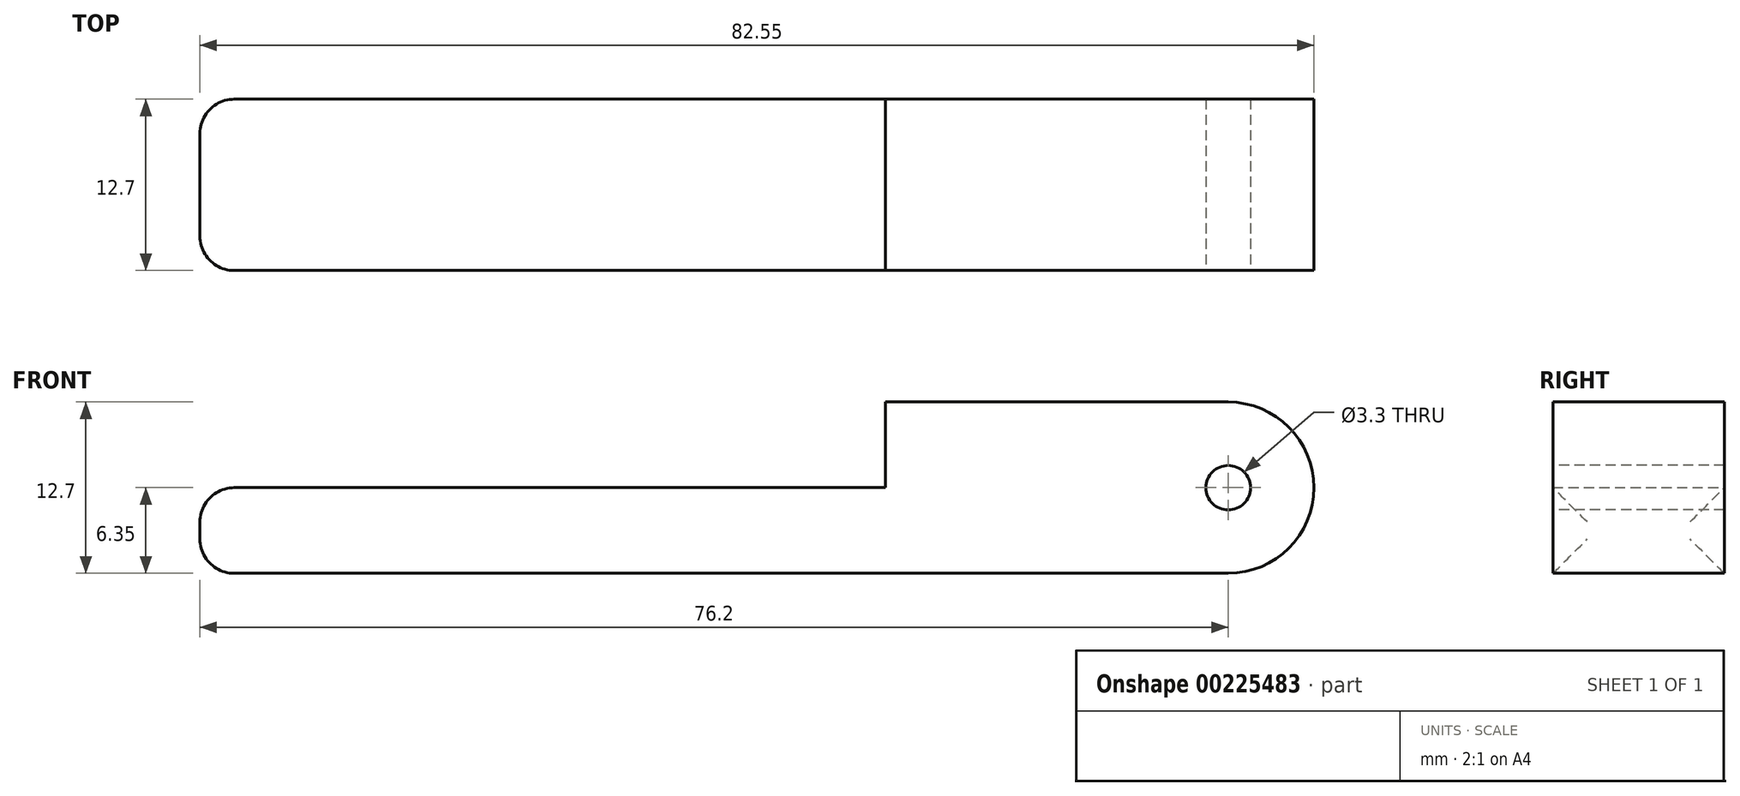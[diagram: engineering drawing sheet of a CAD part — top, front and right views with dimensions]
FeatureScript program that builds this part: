
annotation { "Feature Type Name" : "Feature", "Feature Type Description" : "" }
export const myFeature = defineFeature(function(context is Context, id is Id, definition is map)
    precondition{}
    {
        {
            var Q0;
            Q0=qCreatedBy(makeId("Front.planeOp"),FACE);
            var sketch = newSketch(context, id + "F0", { "sketchPlane" : qUnion([Q0])});
            skLineSegment(sketch, "E0.bottom", {"start": v(0, 0) * mm, "end": v(25.4, 0) * mm});
            skLineSegment(sketch, "E0.top", {"start": v(0, 12.7) * mm, "end": v(25.4, 12.7) * mm});
            skArc(sketch, "E1", {"start": v(25.4, 0) * mm, "mid": v(31.75, 6.35) * mm, "end": v(25.4, 12.7) * mm});
            skLineSegment(sketch, "E2", {"start": v(0, 12.7) * mm, "end": v(0, 6.35) * mm});
            skLineSegment(sketch, "E3", {"start": v(0, 6.35) * mm, "end": v(-50.8, 6.35) * mm});
            skLineSegment(sketch, "E4", {"start": v(-50.8, 6.35) * mm, "end": v(-50.8, 0) * mm});
            skLineSegment(sketch, "E5", {"start": v(-50.8, 0) * mm, "end": v(0, 0) * mm});
            skSolve(sketch);
        }
        {
            var Q0;
            Q0=makeQuery(id+"F0.imprint","IMPRINT",FACE,{"disambiguationData":[TD([[makeQuery(id+"F0.imprint","IMPRINT",EDGE,{"derivedFrom":sQuery(id+"F0.wireOp",EDGE,"E0.bottom")}),1.0]])]});
            extrude(context, id + "F1", {"entities" : qUnion([Q0]), "depth" : 12.7 * mm});
        }
        {
            var Q0;
            Q0=makeQuery(id+"F1.opExtrude","CAP_FACE",FACE,{"disambiguationData":[OSD([sQuery(id+"F0.wireOp",EDGE,"E0.bottom"),sQuery(id+"F0.wireOp",EDGE,"E0.top"),sQuery(id+"F0.wireOp",EDGE,"E1"),sQuery(id+"F0.wireOp",EDGE,"oo02UOLl-CQ9t-fTOI-LPqi-oWK1RCJUGGzr"),sQuery(id+"F0.wireOp",EDGE,"xPii8opp-0xPU-Fjls-u8FU-vih0i7JA0VZS"),sQuery(id+"F0.wireOp",EDGE,"xtSEh5Ry-UN4t-xGok-7Vhy-ALpUBLbRrmse"),sQuery(id+"F0.wireOp",EDGE,"ptmMt4ty-NG1s-mCMr-nPer-JCH92L4xZSmj")])],"isStart":false});
            var sketch = newSketch(context, id + "F2", { "sketchPlane" : qUnion([Q0])});
            skPoint(sketch, "E6", {"position": v(25.4, 6.35) * mm});
            skSolve(sketch);
        }
        {
            var Q0;
            Q0=sQuery(id+"F2.wireOp",VERTEX,"E6");
            var Q1;
            Q1=makeQuery(id+"F1.opExtrude","SWEPT_BODY",BODY,{"disambiguationData":[OSD([sQuery(id+"F0.wireOp",EDGE,"E0.bottom"),sQuery(id+"F0.wireOp",EDGE,"E0.top"),sQuery(id+"F0.wireOp",EDGE,"E1"),sQuery(id+"F0.wireOp",EDGE,"oo02UOLl-CQ9t-fTOI-LPqi-oWK1RCJUGGzr"),sQuery(id+"F0.wireOp",EDGE,"xPii8opp-0xPU-Fjls-u8FU-vih0i7JA0VZS"),sQuery(id+"F0.wireOp",EDGE,"xtSEh5Ry-UN4t-xGok-7Vhy-ALpUBLbRrmse"),sQuery(id+"F0.wireOp",EDGE,"ptmMt4ty-NG1s-mCMr-nPer-JCH92L4xZSmj")])]});
            hole(context, id + "F3", {"style" : HoleStyle.C_BORE, "endStyle" : HoleEndStyle.THROUGH, "holeDiameter" : 3.3 * mm, "cBoreDiameter" : 6.5 * mm, "cBoreDepth" : 0 * mm, "startFromSketch" : true, "locations" : qUnion([Q0]), "scope" : qUnion([Q1]), "isTappedThrough" : true});
        }
        {
            var Q0;
            Q0=makeQuery(id+"F1.opExtrude","SWEPT_FACE",FACE,{"disambiguationData":[OSD([sQuery(id+"F0.wireOp",EDGE,"E4")])]});
            fillet(context, id + "F4", {"entities" : qUnion([Q0]), "radius" : 2.54 * mm, "tangentPropagation" : true, "allowEdgeOverflow" : false});
        }
    });
